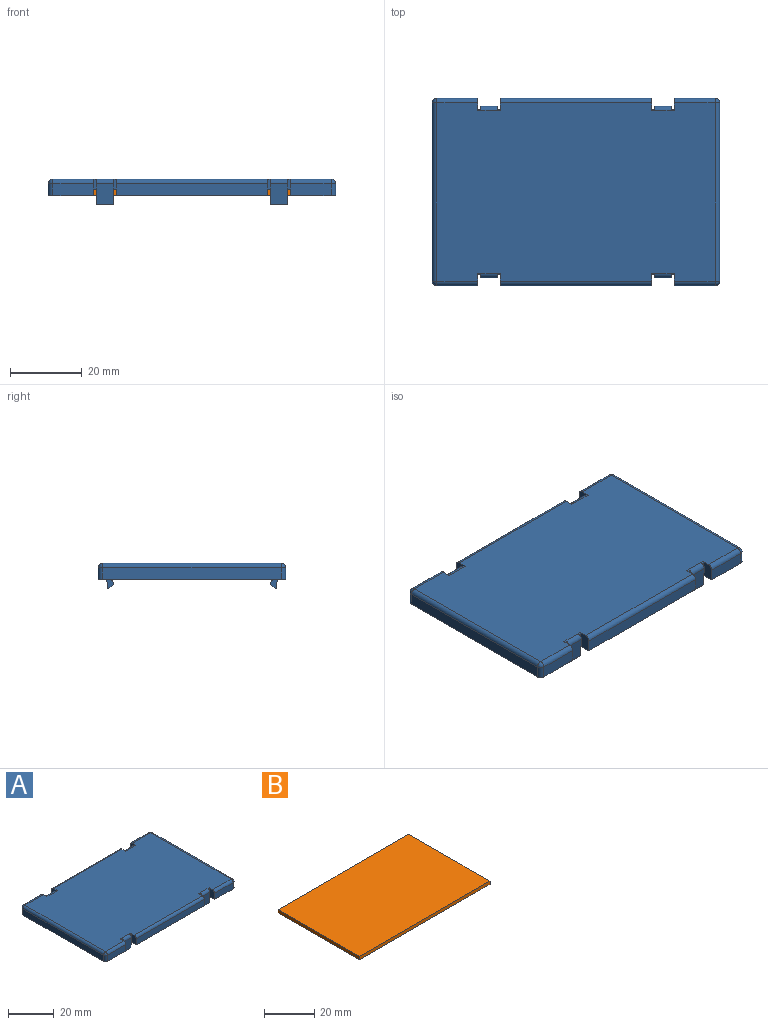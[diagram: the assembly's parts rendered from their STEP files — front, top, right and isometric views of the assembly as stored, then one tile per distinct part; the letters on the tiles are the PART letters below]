
ASSEMBLY  parts=2 mates=1
PART A: 98 faces, bbox 80.3x52.3x7.2 mm
  f0: plane 42.16x1.59mm, normal (0,-1,0), area 66.9mm2, adj f5,f20,f47,f58
  f1: plane 42.16x3.32mm, normal (0,1,0), area 139.9mm2, adj f5,f47,f58,f71
  f2: plane 52.32x12.7mm, normal (0,0,-1), area 225.9mm2, adj f11,f12,f14,f15,f16,f18,f34,f59
  f3: plane 9.53x1.59mm, normal (0,-1,0), area 15.1mm2, adj f17,f19,f20,f46
  f4: plane 11.43x3.32mm, normal (0,1,0), area 37.9mm2, adj f19,f46,f76,f79
  f5: plane 42.16x3.18mm, normal (0,0,-1), area 133.9mm2, adj f0,f1,f47,f58
  f6: plane 42.16x3.32mm, normal (0,-1,0), area 139.9mm2, adj f8,f22,f35,f81
  f7: plane 42.16x1.59mm, normal (0,1,0), area 66.9mm2, adj f8,f20,f22,f35
  f8: plane 42.16x3.18mm, normal (0,0,-1), area 133.9mm2, adj f6,f7,f22,f35
  f9: plane 11.43x3.32mm, normal (0,-1,0), area 37.9mm2, adj f19,f23,f73,f74
  f10: plane 9.53x1.59mm, normal (0,1,0), area 15.1mm2, adj f17,f19,f20,f23
  f11: plane 49.78x3.32mm, normal (-1,0,0), area 165.2mm2, adj f2,f83,f86,f87
  f12: plane 11.43x3.32mm, normal (0,-1,0), area 37.9mm2, adj f2,f34,f86,f89
  f13: plane 49.78x3.32mm, normal (1,0,0), area 165.2mm2, adj f19,f73,f76,f77
  f14: plane 9.53x1.59mm, normal (0,1,0), area 15.1mm2, adj f2,f15,f20,f34
  f15: plane 45.97x1.59mm, normal (1,0,0), area 73mm2, adj f2,f14,f16,f20
  f16: plane 9.53x1.59mm, normal (0,-1,0), area 15.1mm2, adj f2,f15,f20,f59
  f17: plane 45.97x1.59mm, normal (-1,0,0), area 73mm2, adj f3,f10,f19,f20
  f18: plane 11.43x3.32mm, normal (0,1,0), area 37.9mm2, adj f2,f59,f83,f84
  f19: plane 52.32x12.7mm, normal (0,0,-1), area 225.9mm2, adj f3,f4,f9,f10,f13,f17,f23,f46
  f20: plane 73.91x45.97mm, normal (0,0,-1), area 3398.1mm2, adj f0,f3,f7,f10,f14,f15,f16,f17
  f21: plane 77.72x49.78mm, normal (0,0,1), area 3813.4mm2, adj f22,f23,f34,f35,f46,f47,f58,f59
  f22: plane 4.59x3.48mm, normal (1,0,0), area 14.2mm2, adj f6,f7,f8,f21,f24,f81,f82
  f23: plane 4.59x3.48mm, normal (-1,0,0), area 14.2mm2, adj f9,f10,f19,f21,f24,f74,f82
  f24: plane 6.35x2.96mm, normal (0,-1,0), area 13.4mm2, adj f20,f22,f23,f31,f32,f33,f82
  f25: plane 5.75x4.83mm, normal (0,-1,-0.06), area 27.8mm2, adj f32,f33,f82,f96
  f26: plane 4.83x0.17mm, normal (0,0,-1), area 0.8mm2, adj f32,f33,f96,f97
  f27: plane 4.83x1.28mm, normal (0,0.71,-0.71), area 8.7mm2, adj f28,f32,f33,f97
  f28: extruded ~4.83x1.31mm, area 9.2mm2, adj f27,f29,f32,f33
  f29: plane 4.83x0.03mm, normal (0,0,1), area 0.1mm2, adj f28,f30,f32,f33
  f30: plane 4.83x3.42mm, normal (0,1,0), area 16.5mm2, adj f29,f31,f32,f33
  f31: plane 4.83x0.03mm, normal (0,0,-1), area 0.1mm2, adj f24,f30,f32,f33
  f32: plane 7.17x1.99mm, normal (1,0,0), area 7.2mm2, adj f24,f25,f26,f27,f28,f29,f30,f31
  f33: plane 7.17x1.99mm, normal (-1,0,0), area 7.2mm2, adj f24,f25,f26,f27,f28,f29,f30,f31
  f34: plane 4.59x3.48mm, normal (1,0,0), area 14.2mm2, adj f2,f12,f14,f21,f36,f80,f89
  f35: plane 4.59x3.48mm, normal (-1,0,0), area 14.2mm2, adj f6,f7,f8,f21,f36,f80,f81
  f36: plane 6.35x2.96mm, normal (0,-1,0), area 13.4mm2, adj f20,f34,f35,f37,f38,f39,f80
  f37: plane 4.83x0.03mm, normal (0,0,-1), area 0.1mm2, adj f36,f38,f39,f40
  f38: plane 7.17x1.99mm, normal (-1,0,0), area 7.2mm2, adj f36,f37,f40,f41,f42,f43,f44,f45
  f39: plane 7.17x1.99mm, normal (1,0,0), area 7.2mm2, adj f36,f37,f40,f41,f42,f43,f44,f45
  f40: plane 4.83x3.42mm, normal (0,1,0), area 16.5mm2, adj f37,f38,f39,f41
  f41: plane 4.83x0.03mm, normal (0,0,1), area 0.1mm2, adj f38,f39,f40,f42
  f42: extruded ~4.83x1.31mm, area 9.2mm2, adj f38,f39,f41,f43
  f43: plane 4.83x1.28mm, normal (0,0.71,-0.71), area 8.7mm2, adj f38,f39,f42,f95
  f44: plane 4.83x0.17mm, normal (0,0,-1), area 0.8mm2, adj f38,f39,f94,f95
  f45: plane 5.75x4.83mm, normal (0,-1,-0.06), area 27.8mm2, adj f38,f39,f80,f94
  f46: plane 4.59x3.48mm, normal (-1,0,0), area 14.2mm2, adj f3,f4,f19,f21,f48,f72,f79
  f47: plane 4.59x3.48mm, normal (1,0,0), area 14.2mm2, adj f0,f1,f5,f21,f48,f71,f72
  f48: plane 6.35x2.96mm, normal (0,1,0), area 13.4mm2, adj f20,f46,f47,f49,f50,f51,f72
  f49: plane 4.83x0.03mm, normal (0,0,-1), area 0.1mm2, adj f48,f50,f51,f52
  f50: plane 7.17x1.99mm, normal (1,0,0), area 7.2mm2, adj f48,f49,f52,f53,f54,f55,f56,f57
  f51: plane 7.17x1.99mm, normal (-1,0,0), area 7.2mm2, adj f48,f49,f52,f53,f54,f55,f56,f57
  f52: plane 4.83x3.42mm, normal (0,-1,0), area 16.5mm2, adj f49,f50,f51,f53
  f53: plane 4.83x0.03mm, normal (0,0,1), area 0.1mm2, adj f50,f51,f52,f54
  f54: extruded ~4.83x1.31mm, area 9.2mm2, adj f50,f51,f53,f55
  f55: plane 4.83x1.28mm, normal (0,-0.71,-0.71), area 8.7mm2, adj f50,f51,f54,f93
  f56: plane 4.83x0.17mm, normal (0,0,-1), area 0.8mm2, adj f50,f51,f92,f93
  f57: plane 5.75x4.83mm, normal (0,1,-0.06), area 27.8mm2, adj f50,f51,f72,f92
  f58: plane 4.59x3.48mm, normal (-1,0,0), area 14.2mm2, adj f0,f1,f5,f21,f60,f70,f71
  f59: plane 4.59x3.48mm, normal (1,0,0), area 14.2mm2, adj f2,f16,f18,f21,f60,f70,f84
  f60: plane 6.35x2.96mm, normal (0,1,0), area 13.4mm2, adj f20,f58,f59,f67,f68,f69,f70
  f61: plane 5.75x4.83mm, normal (0,1,-0.06), area 27.8mm2, adj f68,f69,f70,f90
  f62: plane 4.83x0.17mm, normal (0,0,-1), area 0.8mm2, adj f68,f69,f90,f91
  f63: plane 4.83x1.28mm, normal (0,-0.71,-0.71), area 8.7mm2, adj f64,f68,f69,f91
  f64: extruded ~4.83x1.31mm, area 9.2mm2, adj f63,f65,f68,f69
  f65: plane 4.83x0.03mm, normal (0,0,1), area 0.1mm2, adj f64,f66,f68,f69
  f66: plane 4.83x3.42mm, normal (0,-1,0), area 16.5mm2, adj f65,f67,f68,f69
  f67: plane 4.83x0.03mm, normal (0,0,-1), area 0.1mm2, adj f60,f66,f68,f69
  f68: plane 7.17x1.99mm, normal (-1,0,0), area 7.2mm2, adj f60,f61,f62,f63,f64,f65,f66,f67
  f69: plane 7.17x1.99mm, normal (1,0,0), area 7.2mm2, adj f60,f61,f62,f63,f64,f65,f66,f67
  f70: cylinder r=1.27mm len=6.35mm, axis (1,0,0), area 10.4mm2, adj f21,f58,f59,f60,f61,f68,f69
  f71: cylinder r=1.27mm len=42.16mm, axis (1,0,0), area 84.1mm2, adj f1,f21,f47,f58
  f72: cylinder r=1.27mm len=6.35mm, axis (1,0,0), area 10.4mm2, adj f21,f46,f47,f48,f50,f51,f57
  f73: cylinder r=1.27mm len=3.32mm, axis (0,0,1), area 6.6mm2, adj f9,f13,f19,f75
  f74: cylinder r=1.27mm len=11.43mm, axis (-1,0,0), area 22.8mm2, adj f9,f21,f23,f75
  f75: sphere r=1.27mm, area 2.5mm2, adj f73,f74,f77
  f76: cylinder r=1.27mm len=3.32mm, axis (0,0,-1), area 6.6mm2, adj f4,f13,f19,f78
  f77: cylinder r=1.27mm len=49.78mm, axis (0,-1,0), area 99.3mm2, adj f13,f21,f75,f78
  f78: sphere r=1.27mm, area 2.5mm2, adj f76,f77,f79
  f79: cylinder r=1.27mm len=11.43mm, axis (1,0,0), area 22.8mm2, adj f4,f21,f46,f78
  f80: cylinder r=1.27mm len=6.35mm, axis (-1,0,0), area 10.4mm2, adj f21,f34,f35,f36,f38,f39,f45
  f81: cylinder r=1.27mm len=42.16mm, axis (-1,0,0), area 84.1mm2, adj f6,f21,f22,f35
  f82: cylinder r=1.27mm len=6.35mm, axis (-1,0,0), area 10.4mm2, adj f21,f22,f23,f24,f25,f32,f33
  f83: cylinder r=1.27mm len=3.32mm, axis (0,0,1), area 6.6mm2, adj f2,f11,f18,f85
  f84: cylinder r=1.27mm len=11.43mm, axis (1,0,0), area 22.8mm2, adj f18,f21,f59,f85
  f85: sphere r=1.27mm, area 2.5mm2, adj f83,f84,f87
  f86: cylinder r=1.27mm len=3.32mm, axis (0,0,-1), area 6.6mm2, adj f2,f11,f12,f88
  f87: cylinder r=1.27mm len=49.78mm, axis (0,1,0), area 99.3mm2, adj f11,f21,f85,f88
  f88: sphere r=1.27mm, area 2.5mm2, adj f86,f87,f89
  f89: cylinder r=1.27mm len=11.43mm, axis (-1,0,0), area 22.8mm2, adj f12,f21,f34,f88
  f90: cylinder r=0.13mm len=4.83mm, axis (1,0,0), area 0.9mm2, adj f61,f62,f68,f69
  f91: cylinder r=0.13mm len=4.83mm, axis (1,0,0), area 0.5mm2, adj f62,f63,f68,f69
  f92: cylinder r=0.13mm len=4.83mm, axis (-1,0,0), area 0.9mm2, adj f50,f51,f56,f57
  f93: cylinder r=0.13mm len=4.83mm, axis (-1,0,0), area 0.5mm2, adj f50,f51,f55,f56
  f94: cylinder r=0.13mm len=4.83mm, axis (1,0,0), area 0.9mm2, adj f38,f39,f44,f45
  f95: cylinder r=0.13mm len=4.83mm, axis (1,0,0), area 0.5mm2, adj f38,f39,f43,f44
  f96: cylinder r=0.13mm len=4.83mm, axis (-1,0,0), area 0.9mm2, adj f25,f26,f32,f33
  f97: cylinder r=0.13mm len=4.83mm, axis (-1,0,0), area 0.5mm2, adj f26,f27,f32,f33
PART B: 6 faces, bbox 73.7x45.7x1.6 mm
  f0: plane 73.66x1.59mm, normal (0,1,0), area 116.9mm2, adj f1,f3,f4,f5
  f1: plane 45.72x1.59mm, normal (-1,0,0), area 72.6mm2, adj f0,f2,f4,f5
  f2: plane 73.66x1.59mm, normal (0,-1,0), area 116.9mm2, adj f1,f3,f4,f5
  f3: plane 45.72x1.59mm, normal (1,0,0), area 72.6mm2, adj f0,f2,f4,f5
  f4: plane 73.66x45.72mm, normal (0,0,1), area 3367.7mm2, adj f0,f1,f2,f3
  f5: plane 73.66x45.72mm, normal (0,0,-1), area 3367.7mm2, adj f0,f1,f2,f3
PLACE A t=(0.05,-0.01,-1.11)mm
PLACE B t=(1.7,-0.01,-1.11)mm
MATE fastened B.f4 <-> A.f20  axis (0,0,1) through (0.05,-0.01,0.47)mm
